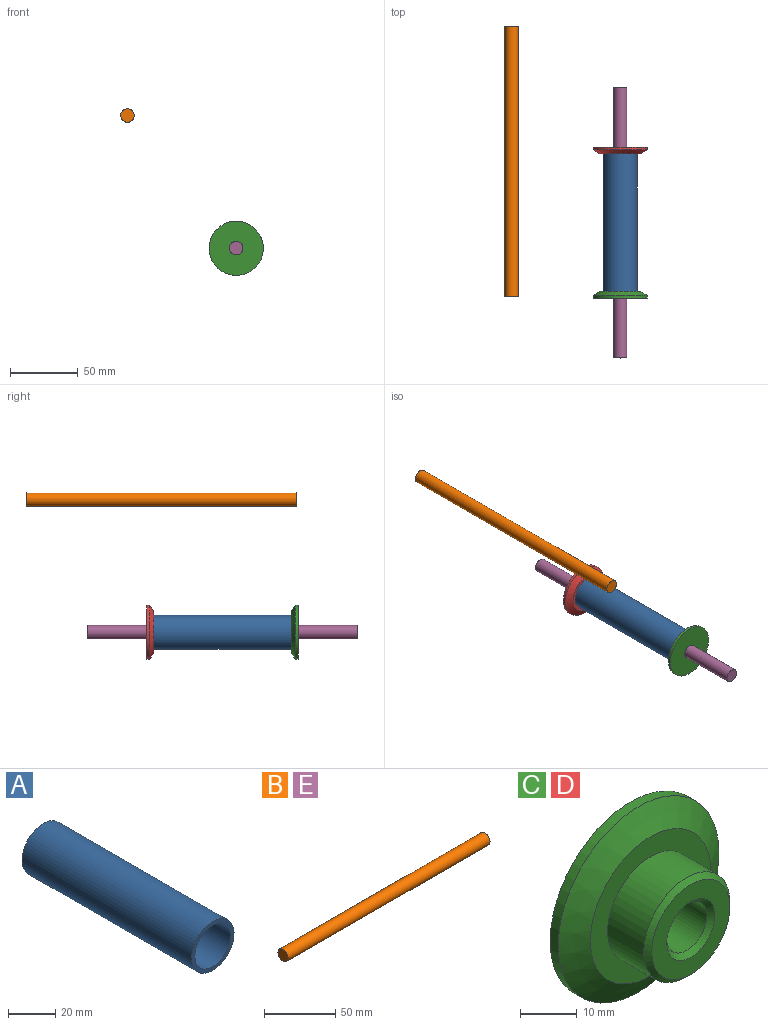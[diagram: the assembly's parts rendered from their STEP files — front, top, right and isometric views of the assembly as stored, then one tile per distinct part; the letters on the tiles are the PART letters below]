
ASSEMBLY  parts=5 mates=3
PART A: 4 faces, bbox 25.4x101.6x25.4 mm
  f0: cylinder r=10.7mm len=101.6mm, axis (0,1,0), area 6830.6mm2, adj f2,f3
  f1: cylinder r=12.7mm len=101.6mm, axis (0,1,0), area 8107.3mm2, adj f2,f3
  f2: plane 25.4x25.4mm, normal (0,-1,0), area 147mm2, adj f0,f1
  f3: plane 25.4x25.4mm, normal (0,1,0), area 147mm2, adj f0,f1
PART B: 3 faces, bbox 200x10x10 mm
  f0: cylinder r=5mm len=200mm, axis (-1,0,0), area 6283.2mm2, adj f1,f2
  f1: plane 10x10mm, normal (1,0,0), area 78.5mm2, adj f0
  f2: plane 10x10mm, normal (-1,0,0), area 78.5mm2, adj f0
PART C: 9 faces, bbox 40x15x40 mm
  f0: cylinder r=5mm len=14mm, axis (0,1,0), area 439.8mm2, adj f3,f7
  f1: cylinder r=10.7mm len=21.4mm, axis (0,1,0), area 605.1mm2, adj f6,f8
  f2: plane 19.4x19.4mm, normal (0,-1,0), area 182.5mm2, adj f7,f8
  f3: plane 40x40mm, normal (0,1,0), area 1178.1mm2, adj f0,f4
  f4: cylinder r=20mm len=40mm, axis (0,1,0), area 251.3mm2, adj f3,f5
  f5: cone r=15mm half-angle=59deg, axis (0,1,0), area 641.1mm2, adj f4,f6
  f6: plane 30x30mm, normal (0,-1,0), area 347.2mm2, adj f1,f5
  f7: cone r=5mm half-angle=45deg, axis (0,-1,0), area 48.9mm2, adj f0,f2
  f8: cone r=9.7mm half-angle=45deg, axis (0,1,0), area 90.6mm2, adj f1,f2
PART D: same geometry as C
PART E: same geometry as B
PLACE A rot(axis=(0,-1,0),13.5deg) t=(-66.55,-0.71,-212.74)mm
PLACE B rot(axis=(0,0,-1),90deg) t=(-146.88,-11.42,-114.65)mm
PLACE C rot(axis=(-0.99,0,-0.12),180deg) t=(-66.55,-112.31,-212.74)mm
PLACE D rot(axis=(0,-1,0),13.5deg) t=(-66.55,-0.71,-212.74)mm
PLACE E rot(axis=(0,0,1),90deg) t=(-66.55,-56.51,-212.74)mm
MATE revolute A.f1 <-> E.f0  axis (0,1,0) through (-66.55,-56.51,-212.74)mm
MATE fastened D.f1 <-> A.f1  axis (0,-1,0) through (-66.55,-5.71,-212.74)mm
MATE fastened C.f1 <-> A.f0  axis (0,1,0) through (-66.55,-107.31,-212.74)mm
